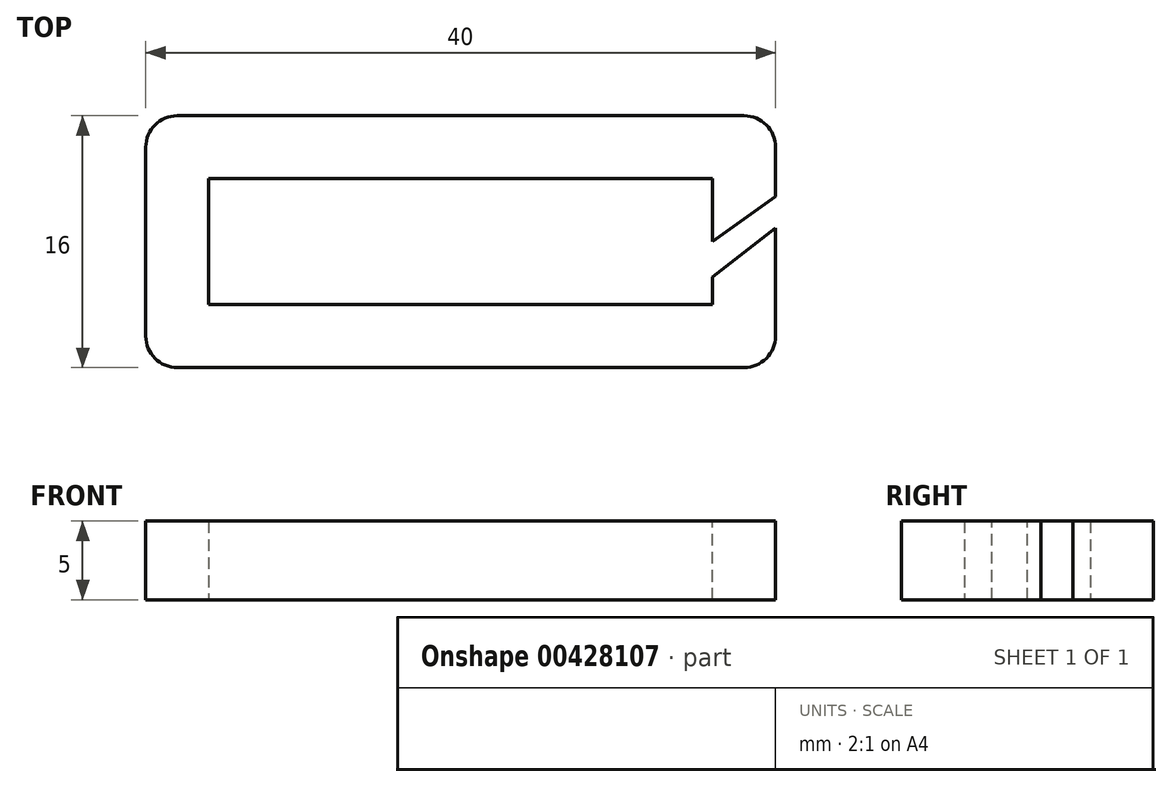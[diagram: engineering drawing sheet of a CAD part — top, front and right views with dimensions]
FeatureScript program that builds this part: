
annotation { "Feature Type Name" : "Feature", "Feature Type Description" : "" }
export const myFeature = defineFeature(function(context is Context, id is Id, definition is map)
    precondition{}
    {
        {
            var Q0;
            Q0=qCreatedBy(makeId("Top.planeOp"),FACE);
            var sketch = newSketch(context, id + "F0", { "sketchPlane" : qUnion([Q0])});
            skLineSegment(sketch, "E0.bottom", {"start": v(-20, 8) * mm, "end": v(20, 8) * mm});
            skLineSegment(sketch, "E0.top", {"start": v(-20, -8) * mm, "end": v(20, -8) * mm});
            skLineSegment(sketch, "E0.left", {"start": v(-20, 8) * mm, "end": v(-20, -8) * mm});
            skLineSegment(sketch, "E0.right", {"start": v(20, 8) * mm, "end": v(20, -8) * mm});
            skPoint(sketch, "E0.middle", {"position": v(0, 0) * mm});
            skLineSegment(sketch, "E1.bottom", {"start": v(16, -4) * mm, "end": v(-16, -4) * mm});
            skLineSegment(sketch, "E1.top", {"start": v(16, 4) * mm, "end": v(-16, 4) * mm});
            skLineSegment(sketch, "E1.left", {"start": v(16, -4) * mm, "end": v(16, 4) * mm});
            skLineSegment(sketch, "E1.right", {"start": v(-16, -4) * mm, "end": v(-16, 4) * mm});
            skSolve(sketch);
        }
        {
            var Q0;
            Q0=makeQuery(id+"F0.imprint","IMPRINT",FACE,{"disambiguationData":[TD([[makeQuery(id+"F0.imprint","IMPRINT",EDGE,{"derivedFrom":sQuery(id+"F0.wireOp",EDGE,"E0.bottom")}),-1.0]])]});
            extrude(context, id + "F1", {"entities" : qUnion([Q0]), "endBound" : BoundingType.SYMMETRIC, "depth" : 5 * mm});
        }
        {
            var Q0;
            Q0=makeQuery(id+"F1.opExtrude","SWEPT_EDGE",EDGE,{"disambiguationData":[OSD([sQuery(id+"F0.wireOp",EDGE,"E0.bottom"),sQuery(id+"F0.wireOp",EDGE,"E0.left")])]});
            var Q1;
            Q1=makeQuery(id+"F1.opExtrude","SWEPT_EDGE",EDGE,{"disambiguationData":[OSD([sQuery(id+"F0.wireOp",EDGE,"E0.top"),sQuery(id+"F0.wireOp",EDGE,"E0.left")])]});
            var Q2;
            Q2=makeQuery(id+"F1.opExtrude","SWEPT_EDGE",EDGE,{"disambiguationData":[OSD([sQuery(id+"F0.wireOp",EDGE,"E0.top"),sQuery(id+"F0.wireOp",EDGE,"E0.right")])]});
            var Q3;
            Q3=makeQuery(id+"F1.opExtrude","SWEPT_EDGE",EDGE,{"disambiguationData":[OSD([sQuery(id+"F0.wireOp",EDGE,"E0.bottom"),sQuery(id+"F0.wireOp",EDGE,"E0.right")])]});
            fillet(context, id + "F2", {"entities" : qUnion([Q0, Q1, Q2, Q3]), "radius" : 2 * mm, "tangentPropagation" : true, "allowEdgeOverflow" : false});
        }
        {
            var Q0;
            Q0=makeQuery(id+"F1.opExtrude","CAP_FACE",FACE,{"disambiguationData":[OSD([sQuery(id+"F0.wireOp",EDGE,"E0.bottom"),sQuery(id+"F0.wireOp",EDGE,"E0.top"),sQuery(id+"F0.wireOp",EDGE,"E0.left"),sQuery(id+"F0.wireOp",EDGE,"E0.right"),sQuery(id+"F0.wireOp",EDGE,"E1.bottom"),sQuery(id+"F0.wireOp",EDGE,"E1.top"),sQuery(id+"F0.wireOp",EDGE,"E1.left"),sQuery(id+"F0.wireOp",EDGE,"E1.right")])],"isStart":false});
            var sketch = newSketch(context, id + "F3", { "sketchPlane" : qUnion([Q0])});
            skLineSegment(sketch, "E2", {"start": v(16, -2.26) * mm, "end": v(20, 0.86) * mm});
            skLineSegment(sketch, "E3", {"start": v(20, 0.86) * mm, "end": v(20, 2.87) * mm});
            skLineSegment(sketch, "E4", {"start": v(20, 2.87) * mm, "end": v(16, 0) * mm});
            skLineSegment(sketch, "E5", {"start": v(16, 0) * mm, "end": v(16, -2.26) * mm});
            skSolve(sketch);
        }
        {
            var Q0;
            Q0=makeQuery(id+"F3.imprint","IMPRINT",FACE,{"disambiguationData":[TD([[makeQuery(id+"F3.imprint","IMPRINT",EDGE,{"derivedFrom":sQuery(id+"F3.wireOp",EDGE,"E2")}),1.0]])]});
            extrude(context, id + "F4", {"entities" : qUnion([Q0]), "operationType" : NewBodyOperationType.REMOVE, "endBound" : BoundingType.SYMMETRIC, "oppositeDirection" : true, "depth" : 25 * mm});
        }
    });
